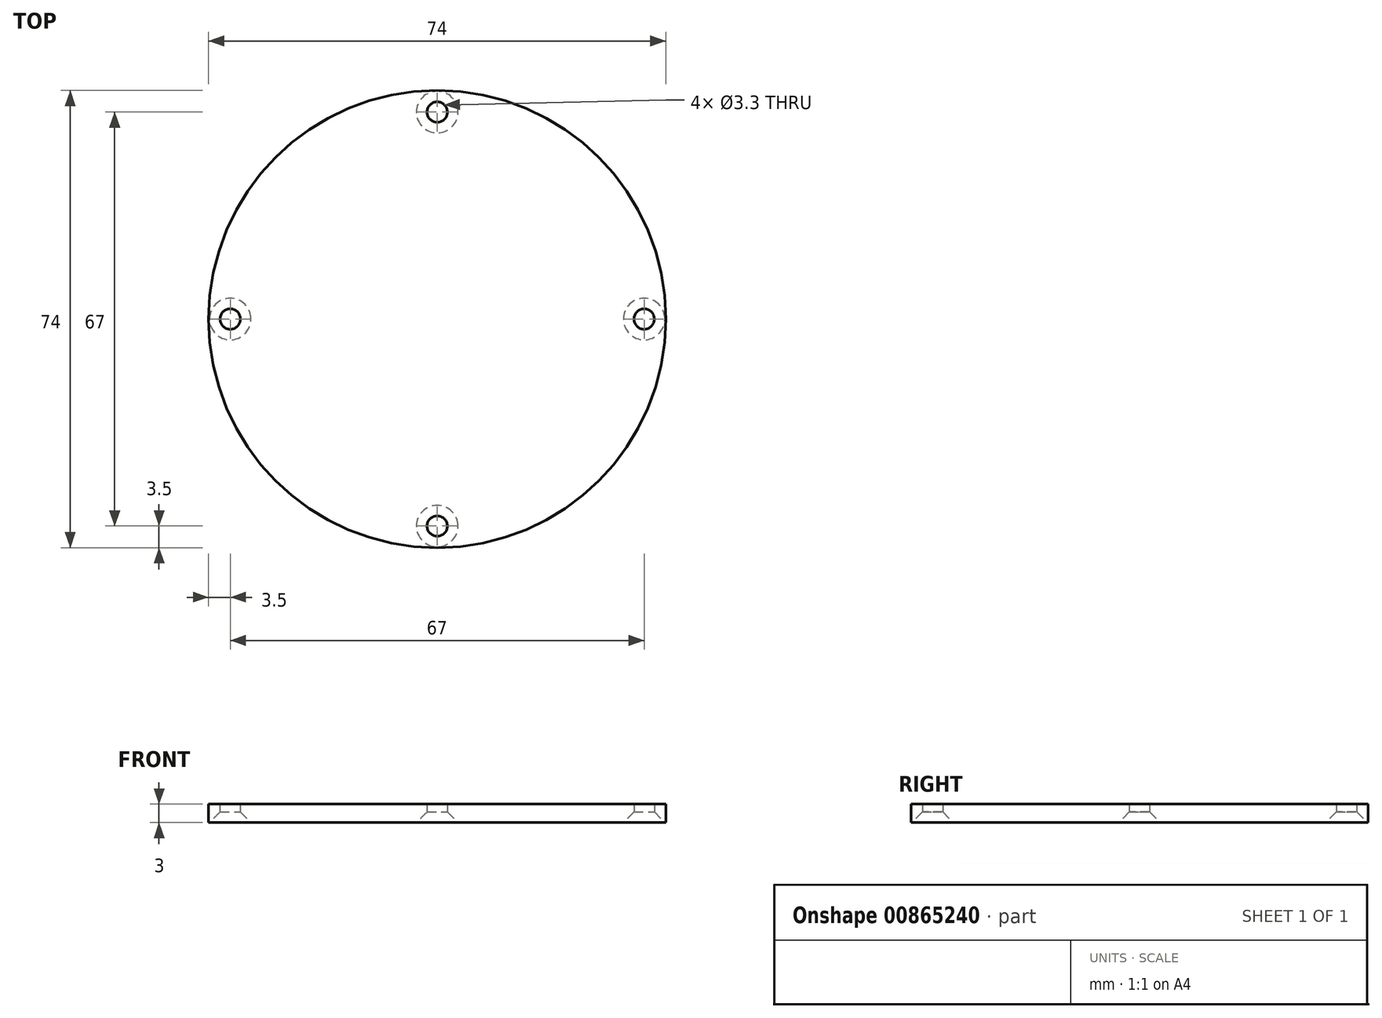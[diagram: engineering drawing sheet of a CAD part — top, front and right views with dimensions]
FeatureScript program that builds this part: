
annotation { "Feature Type Name" : "Feature", "Feature Type Description" : "" }
export const myFeature = defineFeature(function(context is Context, id is Id, definition is map)
    precondition{}
    {
        {
            var Q0;
            Q0=qCreatedBy(makeId("Top.planeOp"),FACE);
            var sketch = newSketch(context, id + "F0", { "sketchPlane" : qUnion([Q0])});
            skCircle(sketch, "E0", {"center": v(0, 0) * mm, "radius": 37 * mm});
            skSolve(sketch);
        }
        {
            var Q0;
            Q0=makeQuery(id+"F0.imprint","IMPRINT",FACE,{"disambiguationData":[TD([[makeQuery(id+"F0.imprint","IMPRINT",EDGE,{"derivedFrom":sQuery(id+"F0.wireOp",EDGE,"E0")}),1.0]])]});
            extrude(context, id + "F1", {"entities" : qUnion([Q0]), "depth" : 3 * mm, "offsetDistance" : 25 * mm});
        }
        {
            var Q0;
            Q0=makeQuery(id+"F1.opExtrude","CAP_FACE",FACE,{"disambiguationData":[OSD([sQuery(id+"F0.wireOp",EDGE,"E0")])],"isStart":true});
            var sketch = newSketch(context, id + "F2", { "sketchPlane" : qUnion([Q0])});
            skCircle(sketch, "E1", {"center": v(0, 0) * mm, "radius": 33.5 * mm});
            skPoint(sketch, "E2", {"position": v(-33.5, 0) * mm});
            skPoint(sketch, "E3", {"position": v(0, 33.5) * mm});
            skPoint(sketch, "E4", {"position": v(33.5, 0) * mm});
            skPoint(sketch, "E5", {"position": v(0, -33.5) * mm});
            skSolve(sketch);
        }
        {
            var Q0;
            Q0=sQuery(id+"F2.wireOp",VERTEX,"E2");
            var Q1;
            Q1=sQuery(id+"F2.wireOp",VERTEX,"E3");
            var Q2;
            Q2=sQuery(id+"F2.wireOp",VERTEX,"E4");
            var Q3;
            Q3=sQuery(id+"F2.wireOp",VERTEX,"E5");
            var Q4;
            Q4=makeQuery(id+"F1.opExtrude","SWEPT_BODY",BODY,{"disambiguationData":[OSD([sQuery(id+"F0.wireOp",EDGE,"E0")])]});
            hole(context, id + "F3", {"style" : HoleStyle.C_SINK, "endStyle" : HoleEndStyle.THROUGH, "standardTappedOrClearance" : lookupTablePath({ "fit" : "Normal", "standard" : "ISO", "size" : "M3", "type" : "Clearance" }), "standardBlindInLast" : lookupTablePath({ "fit" : "Standard", "standard" : "ISO", "size" : "M3", "type" : "Clearance" }), "holeDiameter" : 3.3 * mm, "cSinkDiameter" : 6.72 * mm, "cSinkAngle" : 90 * degree, "majorDiameter" : 5 * mm, "isTappedThrough" : true, "tappedDepth" : 12 * mm, "tapClearance" : 3, "locations" : qUnion([Q0, Q1, Q2, Q3]), "scope" : qUnion([Q4])});
        }
    });
